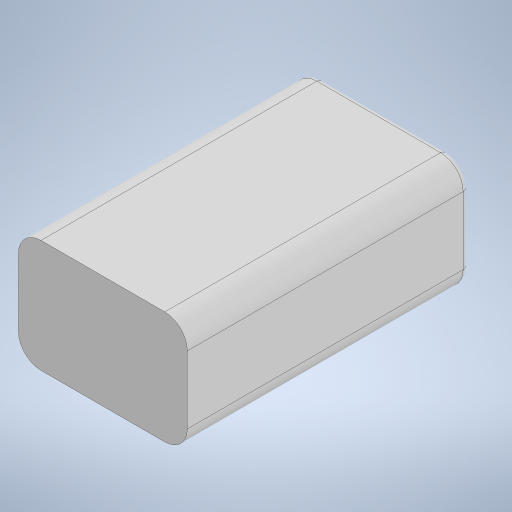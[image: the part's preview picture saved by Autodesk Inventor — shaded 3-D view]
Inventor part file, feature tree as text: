
AUTODESK INVENTOR PART (.ipt)
format: ipt  version: 2023 (Build 270158000, 158)  size: 305,664 bytes
history: native  units: in
note: dims shown in document units (in); Inventor stores cm internally (conversion verified against a paired STEP export)
features: sketch x7, extrude x5, fillet x5, hole x2
ambient origin geometry x8: Origin, YZ Plane, XZ Plane, XY Plane, X Axis, Y Axis, Z Axis, Center Point
bodies: Solid1 (feature_tree)
feature tree (19):
  extrude  "Extrusion1"  Depth=3.937in
  fillet  "Fillet1"  Radius=9.8425in
  fillet  "Fillet2"  Radius=0.7874in
  fillet  "Fillet3"  Radius=0.7874in
  fillet  "Fillet4"  Radius=0.7874in
  fillet  "Fillet5"  Radius=0.7874in
  extrude  "Extrusion2"  Depth=0.9843in
  extrude  "Extrusion3"  Depth=0.1969in
  extrude  "Extrusion4"  Depth=0.3937in
  extrude  "Extrusion5"  Depth=0.1969in
  hole  "Hole1"  [1 undecoded]
  hole  "Hole2"  [1 undecoded]
  sketch  "Sketch1"  dims[d0=5.9055in d1=3.937in d2=9.8425in d3=0.0in d4=0.7874in d5=0.7874in d6=0.7874in d7=0.7874in]
  sketch  "Sketch2"  dims[d8=0.1969in d9=0.9843in]
  sketch  "Sketch3"  dims[d10=0.1969in d11=0.1969in]
  sketch  "Sketch4"  dims[d12=0.9843in d13=0.3937in]
  sketch  "Sketch5"  dims[d14=0.3937in d15=0.1969in]
  sketch  "Sketch6"  dims[d16=0.9843in d17=0.1969in]
  sketch  "Sketch7"  dims[d18=0.1969in d19=0.0in d20=1.9685in d21=1.5748in d22=2.7559in d23=0.9843in d24=0.9843in d25=0.1181in d26=0.0in d27=0.5906in d28=0.5906in d29=0.0in d30=0.7874in d31=0.6693in d32=0.1575in d33=0.0in d34=0.3979in d35=0.9449in d36=0.1575in d37=0.0787in d38=90.0deg d39=1.1024in d40=0.8108in d41=0.4192in d42=0.9449in d43=0.1575in d44=0.0787in d45=90.0deg d46=1.1024in d47=0.8108in]
note: 2 required parameter values undecoded (feature->parameter linkage not recoverable at this tier; creation-order binding heuristic only, values carry confidence <= 0.55)
